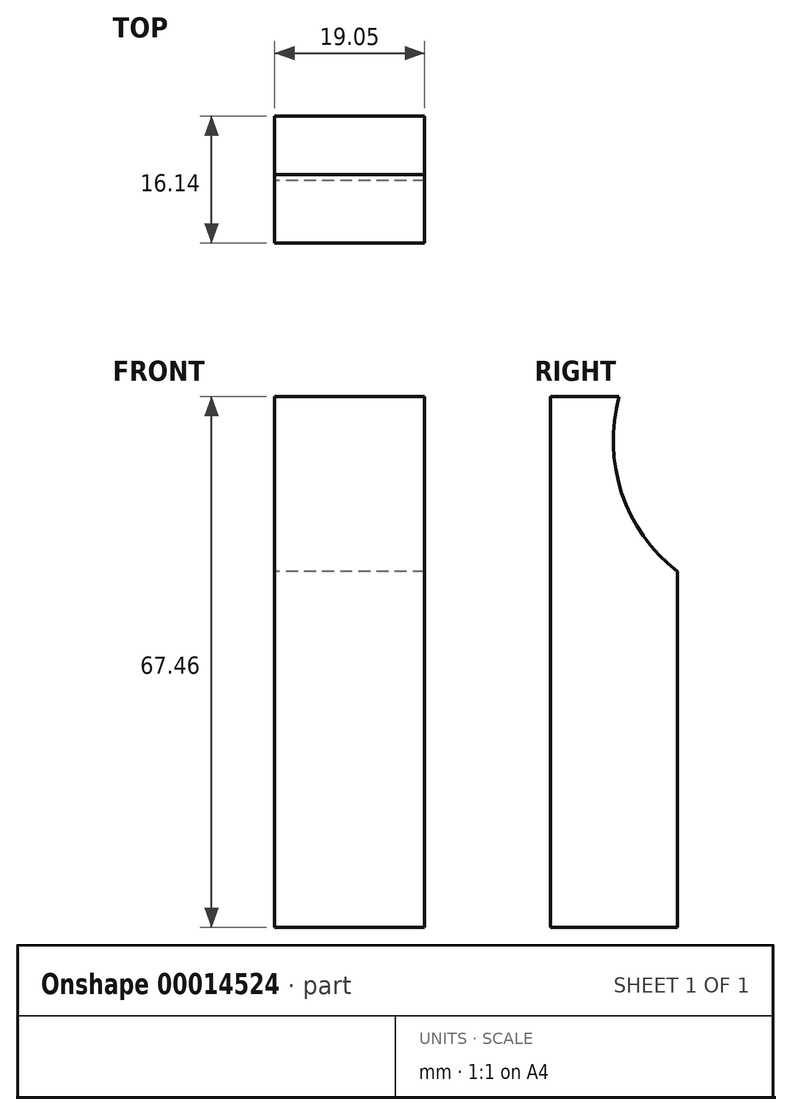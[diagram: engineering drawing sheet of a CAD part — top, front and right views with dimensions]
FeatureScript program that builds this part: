
annotation { "Feature Type Name" : "Feature", "Feature Type Description" : "" }
export const myFeature = defineFeature(function(context is Context, id is Id, definition is map)
    precondition{}
    {
        {
            var Q0;
            Q0=qCreatedBy(makeId("Right.planeOp"),FACE);
            var sketch = newSketch(context, id + "F0", { "sketchPlane" : qUnion([Q0])});
            skLineSegment(sketch, "E0", {"start": v(-5.45, 67.46) * mm, "end": v(-5.45, 0) * mm});
            skLineSegment(sketch, "E1", {"start": v(-5.45, 0) * mm, "end": v(10.69, 0) * mm});
            skLineSegment(sketch, "E2", {"start": v(10.69, 0) * mm, "end": v(10.69, 45.21) * mm});
            skLineSegment(sketch, "E3", {"start": v(-5.45, 67.46) * mm, "end": v(3.27, 67.46) * mm});
            skArc(sketch, "E4", {"start": v(3.27, 67.46) * mm, "mid": v(3.59, 55.2) * mm, "end": v(10.69, 45.21) * mm});
            skSolve(sketch);
        }
        {
            var Q0;
            Q0=makeQuery(id+"F0.imprint","IMPRINT",FACE,{"disambiguationData":[TD([[makeQuery(id+"F0.imprint","IMPRINT",EDGE,{"derivedFrom":sQuery(id+"F0.wireOp",EDGE,"E0")}),1.0]])]});
            extrude(context, id + "F1", {"entities" : qUnion([Q0]), "depth" : 19.05 * mm});
        }
    });
